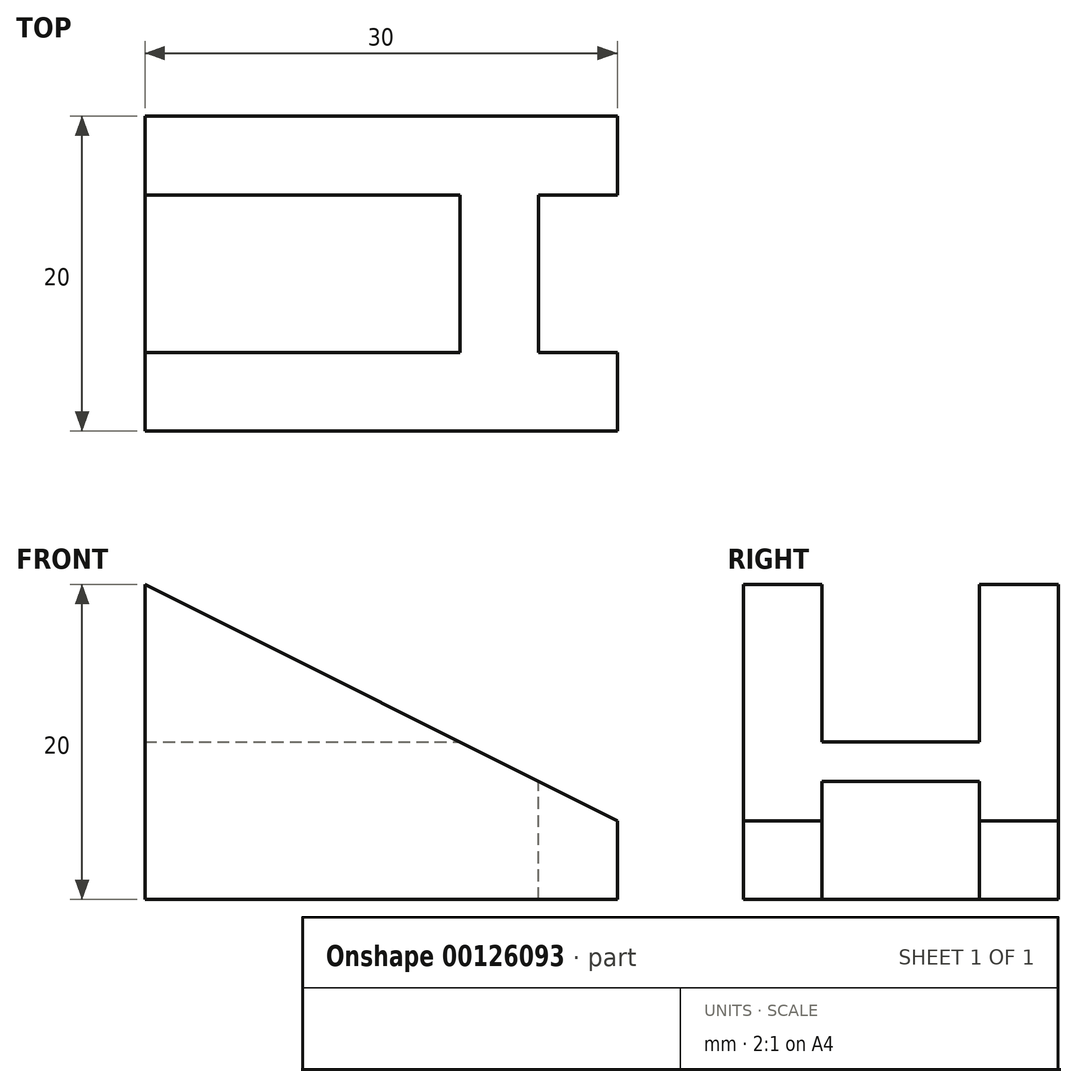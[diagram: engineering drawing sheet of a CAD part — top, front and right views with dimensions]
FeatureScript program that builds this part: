
annotation { "Feature Type Name" : "Feature", "Feature Type Description" : "" }
export const myFeature = defineFeature(function(context is Context, id is Id, definition is map)
    precondition{}
    {
        {
            var Q0;
            Q0=qCreatedBy(makeId("Front.planeOp"),FACE);
            var sketch = newSketch(context, id + "F0", { "sketchPlane" : qUnion([Q0])});
            skLineSegment(sketch, "E0", {"start": v(0, 0) * mm, "end": v(0, 20) * mm});
            skLineSegment(sketch, "E1", {"start": v(0, 0) * mm, "end": v(30, 0) * mm});
            skLineSegment(sketch, "E2", {"start": v(30, 0) * mm, "end": v(30, 5) * mm});
            skLineSegment(sketch, "E3", {"start": v(30, 5) * mm, "end": v(0, 20) * mm});
            skLineSegment(sketch, "E4", {"start": v(25, 0) * mm, "end": v(25, 7.5) * mm});
            skLineSegment(sketch, "E5", {"start": v(0, 10) * mm, "end": v(20, 10) * mm});
            skSolve(sketch);
        }
        {
            var Q0;
            Q0 = qSketchRegion(id + "F0", true);
            extrude(context, id + "F1", {"entities" : qUnion([Q0]), "endBound" : BoundingType.SYMMETRIC, "depth" : 20 * mm});
        }
        {
            var Q0;
            {var subQ3=sQuery(id+"F0.wireOp",EDGE,"E5");Q0=makeQuery(id+"F0.imprint","IMPRINT",FACE,{"disambiguationData":[TD([[makeQuery(id+"F0.imprint","IMPRINT",EDGE,{"derivedFrom":subQ3}),1.0]])]});}
            var Q1;
            {var subQ0=sQuery(id+"F0.wireOp",EDGE,"E2");Q1=makeQuery(id+"F0.imprint","IMPRINT",FACE,{"disambiguationData":[TD([[makeQuery(id+"F0.imprint","IMPRINT",EDGE,{"derivedFrom":subQ0}),1.0]])]});}
            extrude(context, id + "F2", {"entities" : qUnion([Q0, Q1]), "operationType" : NewBodyOperationType.REMOVE, "endBound" : BoundingType.SYMMETRIC, "depth" : 10 * mm});
        }
    });
